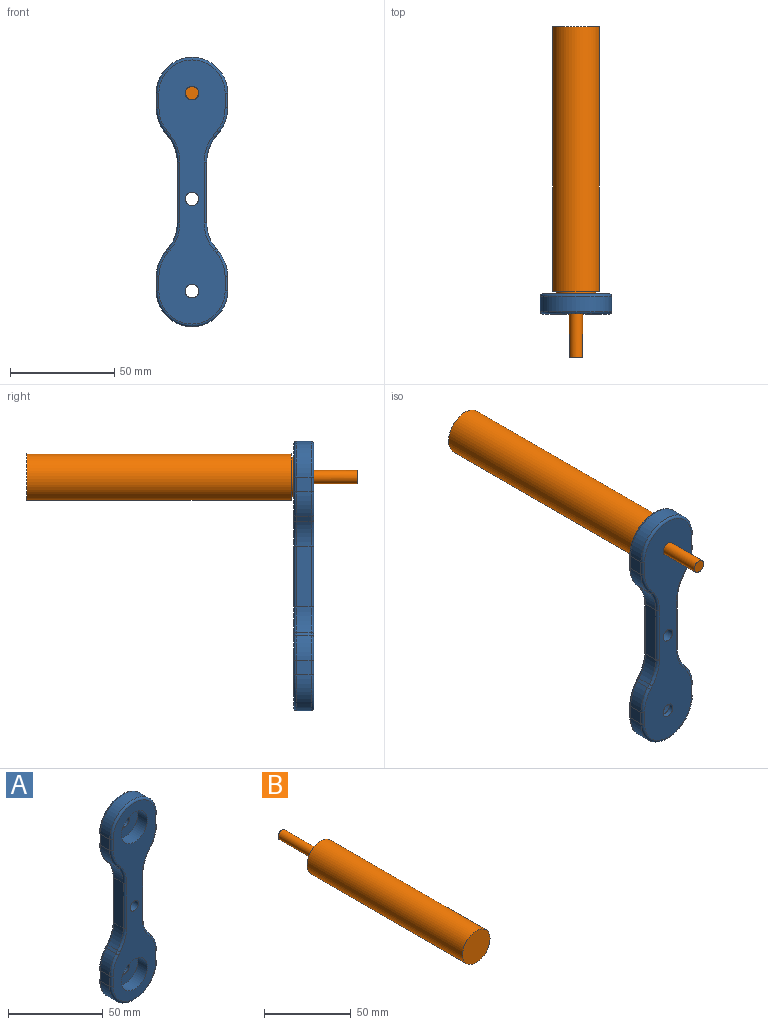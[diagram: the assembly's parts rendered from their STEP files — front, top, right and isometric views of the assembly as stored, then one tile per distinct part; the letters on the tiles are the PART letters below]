
ASSEMBLY  parts=2 mates=1
PART A: 69 faces, bbox 37.4x9.5x132.1 mm
  f0: plane 6.99x6.78mm, normal (-1,0,0), area 47.4mm2, adj f1,f28,f47,f67
  f1: cylinder r=17.14mm len=34.29mm, axis (0,1,0), area 376.2mm2, adj f0,f2,f48,f68
  f2: plane 6.99x6.78mm, normal (1,0,0), area 47.4mm2, adj f1,f21,f46,f66
  f3: plane 6.99x1.42mm, normal (0.77,0,0.64), area 12.9mm2, adj f21,f22,f42,f62
  f4: plane 29.24x6.99mm, normal (1,0,0), area 204.3mm2, adj f22,f23,f38,f58
  f5: plane 6.99x2.5mm, normal (0.79,0,-0.62), area 22.2mm2, adj f23,f24,f34,f54
  f6: plane 7.13x6.99mm, normal (1,0,0), area 49.8mm2, adj f7,f24,f30,f50
  f7: cylinder r=17.14mm len=34.29mm, axis (0,1,0), area 376.2mm2, adj f6,f8,f29,f49
  f8: plane 7.13x6.99mm, normal (-1,0,0), area 49.8mm2, adj f7,f25,f31,f51
  f9: plane 6.99x2.5mm, normal (-0.79,0,-0.62), area 22.2mm2, adj f25,f26,f35,f55
  f10: plane 29.24x6.99mm, normal (-1,0,0), area 204.3mm2, adj f26,f27,f39,f59
  f11: plane 6.99x1.42mm, normal (-0.77,0,0.64), area 12.9mm2, adj f27,f28,f43,f63
  f12: plane 126.75x31.75mm, normal (0,-1,0), area 2068.5mm2, adj f16,f19,f20,f49,f50,f51,f52,f53
  f13: plane 126.75x31.75mm, normal (0,1,0), area 2585.3mm2, adj f14,f17,f20,f29,f30,f31,f32,f33
  f14: cylinder r=3.3mm len=6.6mm, axis (0,-1,0), area 50.1mm2, adj f13,f15
  f15: plane 19.3x19.3mm, normal (0,-1,0), area 258.4mm2, adj f14,f16
  f16: cylinder r=9.65mm len=19.3mm, axis (0,-1,0), area 431.3mm2, adj f12,f15
  f17: cylinder r=3.3mm len=6.6mm, axis (0,-1,0), area 50.1mm2, adj f13,f18
  f18: plane 19.3x19.3mm, normal (0,-1,0), area 258.4mm2, adj f17,f19
  f19: cylinder r=9.65mm len=19.3mm, axis (0,-1,0), area 431.3mm2, adj f12,f18
  f20: cylinder r=3.17mm len=9.53mm, axis (0,-1,0), area 190mm2, adj f12,f13
  f21: cylinder r=19.05mm len=12.22mm, axis (0,1,0), area 92.7mm2, adj f2,f3,f44,f64
  f22: cylinder r=19.05mm len=12.22mm, axis (0,-1,0), area 92.7mm2, adj f3,f4,f40,f60
  f23: cylinder r=19.05mm len=11.74mm, axis (0,-1,0), area 88.4mm2, adj f4,f5,f36,f56
  f24: cylinder r=19.05mm len=11.74mm, axis (0,-1,0), area 88.4mm2, adj f5,f6,f32,f52
  f25: cylinder r=19.05mm len=11.74mm, axis (0,-1,0), area 88.4mm2, adj f8,f9,f33,f53
  f26: cylinder r=19.05mm len=11.74mm, axis (0,1,0), area 88.4mm2, adj f9,f10,f37,f57
  f27: cylinder r=19.05mm len=12.22mm, axis (0,1,0), area 92.7mm2, adj f10,f11,f41,f61
  f28: cylinder r=19.05mm len=12.22mm, axis (0,1,0), area 92.7mm2, adj f0,f11,f45,f65
  f29: torus R=15.88mm, axis (0,-1,0), area 104.6mm2, adj f7,f13,f30,f31
  f30: cylinder r=1.27mm len=7.13mm, axis (0,0,1), area 14.2mm2, adj f6,f13,f29,f32
  f31: cylinder r=1.27mm len=7.13mm, axis (0,0,-1), area 14.2mm2, adj f8,f13,f29,f33
  f32: torus R=17.78mm, axis (0,-1,0), area 24.6mm2, adj f13,f24,f30,f34
  f33: torus R=17.78mm, axis (0,-1,0), area 24.6mm2, adj f13,f25,f31,f35
  f34: cylinder r=1.27mm len=3.28mm, axis (0.62,0,0.79), area 6.3mm2, adj f5,f13,f32,f36
  f35: cylinder r=1.27mm len=3.28mm, axis (0.62,0,-0.79), area 6.3mm2, adj f9,f13,f33,f37
  f36: torus R=20.32mm, axis (0,-1,0), area 25.9mm2, adj f13,f23,f34,f38
  f37: torus R=20.32mm, axis (0,-1,0), area 25.9mm2, adj f13,f26,f35,f39
  f38: cylinder r=1.27mm len=29.24mm, axis (0,0,1), area 58.3mm2, adj f4,f13,f36,f40
  f39: cylinder r=1.27mm len=29.24mm, axis (0,0,-1), area 58.3mm2, adj f10,f13,f37,f41
  f40: torus R=20.32mm, axis (0,-1,0), area 27.1mm2, adj f13,f22,f38,f42
  f41: torus R=20.32mm, axis (0,-1,0), area 27.1mm2, adj f13,f27,f39,f43
  f42: cylinder r=1.27mm len=2.23mm, axis (-0.64,0,0.77), area 3.7mm2, adj f3,f13,f40,f44
  f43: cylinder r=1.27mm len=2.23mm, axis (-0.64,0,-0.77), area 3.7mm2, adj f11,f13,f41,f45
  f44: torus R=17.78mm, axis (0,-1,0), area 25.8mm2, adj f13,f21,f42,f46
  f45: torus R=17.78mm, axis (0,-1,0), area 25.8mm2, adj f13,f28,f43,f47
  f46: cylinder r=1.27mm len=6.78mm, axis (0,0,1), area 13.5mm2, adj f2,f13,f44,f48
  f47: cylinder r=1.27mm len=6.78mm, axis (0,0,-1), area 13.5mm2, adj f0,f13,f45,f48
  f48: torus R=15.88mm, axis (0,-1,0), area 104.6mm2, adj f1,f13,f46,f47
  f49: torus R=15.88mm, axis (0,-1,0), area 104.6mm2, adj f7,f12,f50,f51
  f50: cylinder r=1.27mm len=7.13mm, axis (0,0,-1), area 14.2mm2, adj f6,f12,f49,f52
  f51: cylinder r=1.27mm len=7.13mm, axis (0,0,1), area 14.2mm2, adj f8,f12,f49,f53
  f52: torus R=17.78mm, axis (0,-1,0), area 24.6mm2, adj f12,f24,f50,f54
  f53: torus R=17.78mm, axis (0,-1,0), area 24.6mm2, adj f12,f25,f51,f55
  f54: cylinder r=1.27mm len=3.28mm, axis (-0.62,0,-0.79), area 6.3mm2, adj f5,f12,f52,f56
  f55: cylinder r=1.27mm len=3.28mm, axis (-0.62,0,0.79), area 6.3mm2, adj f9,f12,f53,f57
  f56: torus R=20.32mm, axis (0,-1,0), area 25.9mm2, adj f12,f23,f54,f58
  f57: torus R=20.32mm, axis (0,-1,0), area 25.9mm2, adj f12,f26,f55,f59
  f58: cylinder r=1.27mm len=29.24mm, axis (0,0,-1), area 58.3mm2, adj f4,f12,f56,f60
  f59: cylinder r=1.27mm len=29.24mm, axis (0,0,1), area 58.3mm2, adj f10,f12,f57,f61
  f60: torus R=20.32mm, axis (0,-1,0), area 27.1mm2, adj f12,f22,f58,f62
  f61: torus R=20.32mm, axis (0,-1,0), area 27.1mm2, adj f12,f27,f59,f63
  f62: cylinder r=1.27mm len=2.23mm, axis (0.64,0,-0.77), area 3.7mm2, adj f3,f12,f60,f64
  f63: cylinder r=1.27mm len=2.23mm, axis (0.64,0,0.77), area 3.7mm2, adj f11,f12,f61,f65
  f64: torus R=17.78mm, axis (0,-1,0), area 25.8mm2, adj f12,f21,f62,f66
  f65: torus R=17.78mm, axis (0,-1,0), area 25.8mm2, adj f12,f28,f63,f67
  f66: cylinder r=1.27mm len=6.78mm, axis (0,0,-1), area 13.5mm2, adj f2,f12,f64,f68
  f67: cylinder r=1.27mm len=6.78mm, axis (0,0,1), area 13.5mm2, adj f0,f12,f65,f68
  f68: torus R=15.88mm, axis (0,-1,0), area 104.6mm2, adj f1,f12,f66,f67
PART B: 7 faces, bbox 22.5x158.8x22.5 mm
  f0: cylinder r=11.24mm len=127mm, axis (0,1,0), area 8968.7mm2, adj f1,f2
  f1: plane 22.48x22.48mm, normal (0,-1,0), area 396.9mm2, adj f0
  f2: plane 22.48x22.48mm, normal (0,1,0), area 111.8mm2, adj f0,f3
  f3: cylinder r=9.53mm len=19.05mm, axis (0,-1,0), area 76mm2, adj f2,f4
  f4: plane 19.05x19.05mm, normal (0,1,0), area 253.4mm2, adj f3,f6
  f5: plane 6.35x6.35mm, normal (0,1,0), area 31.7mm2, adj f6
  f6: cylinder r=3.17mm len=30.48mm, axis (0,-1,0), area 608mm2, adj f4,f5
PLACE A rot(axis=(0,0,-1),180deg) t=(0,-0.06,-60.61)mm
PLACE B rot(axis=(0,0,-1),180deg) t=(0,5.97,-9.81)mm
MATE planar B.f3 <-> A.f12  axis (0,-1,0) through (0,4.7,-9.81)mm
